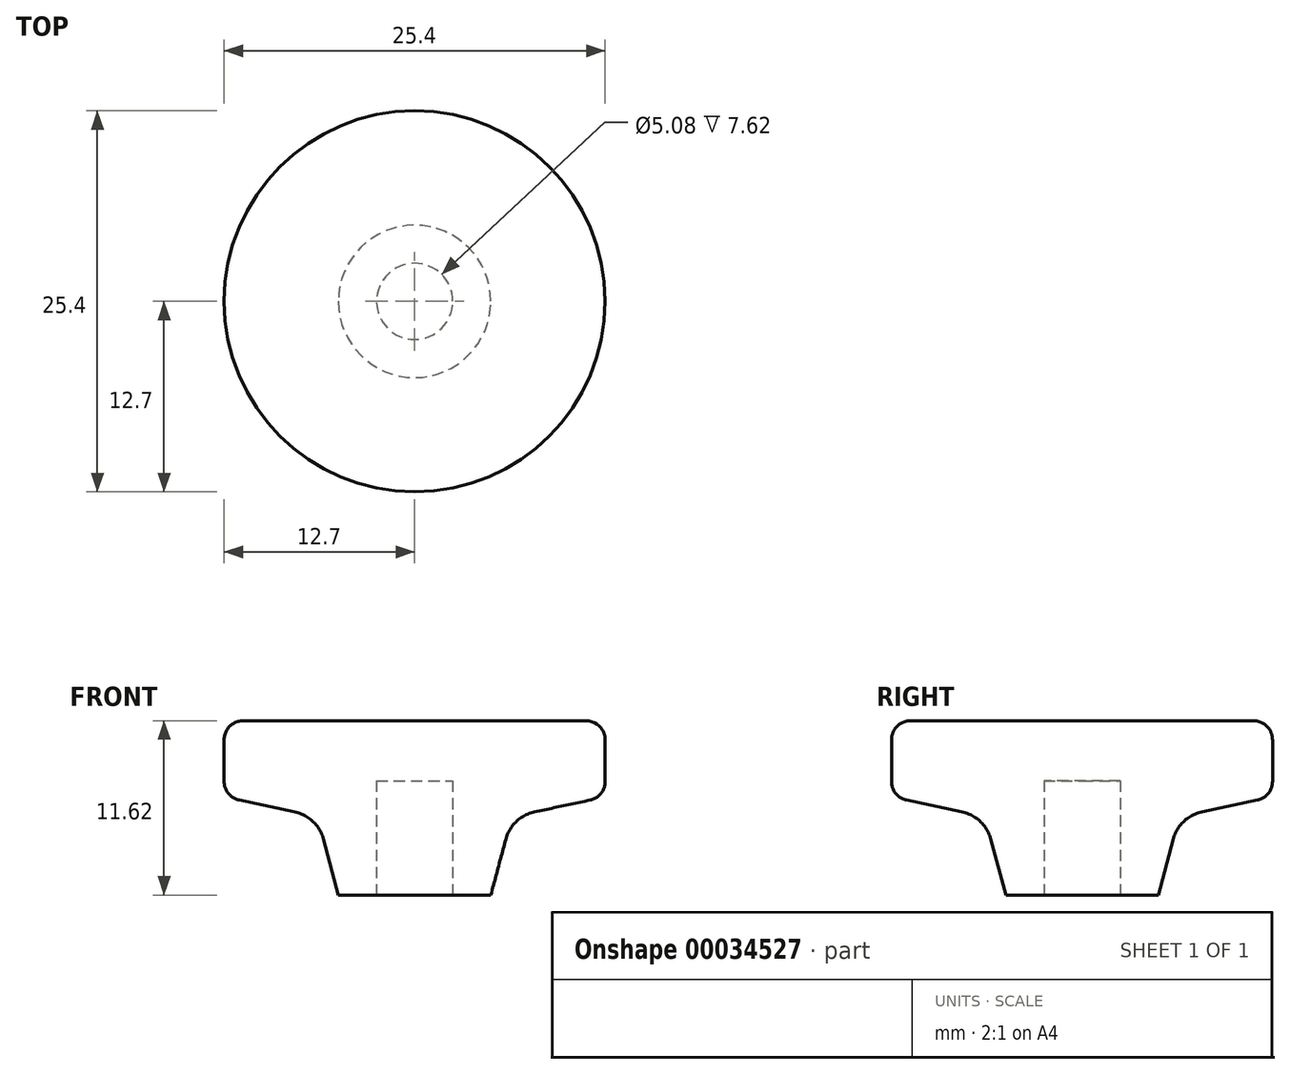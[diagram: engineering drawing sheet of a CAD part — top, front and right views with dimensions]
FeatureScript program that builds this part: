
annotation { "Feature Type Name" : "Feature", "Feature Type Description" : "" }
export const myFeature = defineFeature(function(context is Context, id is Id, definition is map)
    precondition{}
    {
        {
            var Q0;
            Q0=qCreatedBy(makeId("Front.planeOp"),FACE);
            var sketch = newSketch(context, id + "F0", { "sketchPlane" : qUnion([Q0])});
            skLineSegment(sketch, "E0", {"start": v(-12.7, 11.62) * mm, "end": v(-12.7, 6.54) * mm});
            skLineSegment(sketch, "E1", {"start": v(-12.7, 6.54) * mm, "end": v(-6.48, 5.22) * mm});
            skLineSegment(sketch, "E2", {"start": v(-6.48, 5.22) * mm, "end": v(-5.08, 0) * mm});
            skLineSegment(sketch, "E3", {"start": v(-5.08, 0) * mm, "end": v(0, 0) * mm});
            skLineSegment(sketch, "E4", {"start": v(0, 0) * mm, "end": v(0, 11.62) * mm});
            skLineSegment(sketch, "E5", {"start": v(0, 11.62) * mm, "end": v(-12.7, 11.62) * mm});
            skSolve(sketch);
        }
        {
            var Q0;
            Q0=makeQuery(id+"F0.imprint","IMPRINT",FACE,{"disambiguationData":[TD([[makeQuery(id+"F0.imprint","IMPRINT",EDGE,{"derivedFrom":sQuery(id+"F0.wireOp",EDGE,"E0")}),1.0]])]});
            var Q1;
            Q1=sQuery(id+"F0.wireOp",EDGE,"E4");
            revolve(context, id + "F1", {"entities" : qUnion([Q0]), "axis" : qUnion([Q1]), "revolveType" : RevolveType.FULL});
        }
        {
            var Q0;
            Q0=makeQuery(id+"F1.opRevolve","SWEPT_EDGE",EDGE,{"disambiguationData":[OSD([sQuery(id+"F0.wireOp",EDGE,"E1"),sQuery(id+"F0.wireOp",EDGE,"E2")])]});
            fillet(context, id + "F2", {"entities" : qUnion([Q0]), "radius" : 2.54 * mm, "tangentPropagation" : true, "allowEdgeOverflow" : false});
        }
        {
            var Q0;
            Q0=makeQuery(id+"F1.opRevolve","SWEPT_EDGE",EDGE,{"disambiguationData":[OSD([sQuery(id+"F0.wireOp",EDGE,"E0"),sQuery(id+"F0.wireOp",EDGE,"E5")])]});
            var Q1;
            Q1=makeQuery(id+"F1.opRevolve","SWEPT_EDGE",EDGE,{"disambiguationData":[OSD([sQuery(id+"F0.wireOp",EDGE,"E0"),sQuery(id+"F0.wireOp",EDGE,"E1")])]});
            fillet(context, id + "F3", {"entities" : qUnion([Q0, Q1]), "radius" : 1.27 * mm, "tangentPropagation" : true, "allowEdgeOverflow" : false});
        }
        {
            var Q0;
            Q0=makeQuery(id+"F1.opRevolve","SWEPT_FACE",FACE,{"disambiguationData":[OSD([sQuery(id+"F0.wireOp",EDGE,"E3")])]});
            var sketch = newSketch(context, id + "F4", { "sketchPlane" : qUnion([Q0])});
            skCircle(sketch, "E6", {"center": v(0, 0) * mm, "radius": 2.54 * mm});
            skSolve(sketch);
        }
        {
            var Q0;
            Q0 = qSketchRegion(id + "F4", true);
            extrude(context, id + "F5", {"entities" : qUnion([Q0]), "operationType" : NewBodyOperationType.REMOVE, "oppositeDirection" : true, "depth" : 7.62 * mm});
        }
    });
